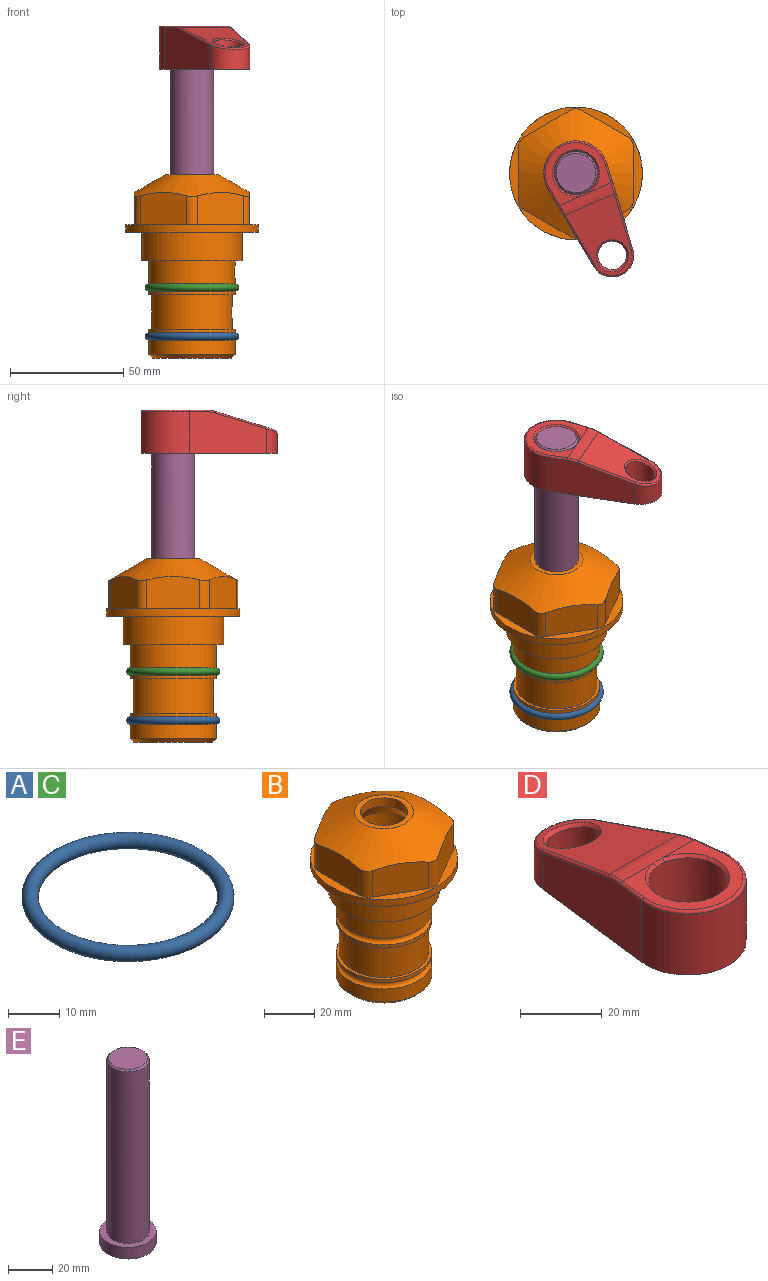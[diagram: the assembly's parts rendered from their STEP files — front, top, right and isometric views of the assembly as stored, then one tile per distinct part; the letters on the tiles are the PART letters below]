
ASSEMBLY  parts=5 mates=4
PART A: 1 faces, bbox 44.7x44.7x3.2 mm
  f0: torus R=19.05mm, axis (0,0,1), area 1193.9mm2
PART B: 36 faces, bbox 58.7x58.7x81 mm
  f0: cylinder r=17.78mm len=35.56mm, axis (0,0,1), area 1670.8mm2, adj f23,f24,f31
  f1: cylinder r=19.05mm len=38.1mm, axis (0,0,1), area 1191.9mm2, adj f26,f27,f30
  f2: plane 58.66x58.66mm, normal (0,0,-1), area 1150.6mm2, adj f3,f28
  f3: cylinder r=29.33mm len=58.66mm, axis (0,0,-1), area 585.1mm2, adj f2,f4
  f4: plane 58.66x58.66mm, normal (0,0,1), area 475.9mm2, adj f3,f5,f6,f7,f8,f9,f10,f11
  f5: plane 20.32x14.34mm, normal (-0.5,0.87,0), area 324.4mm2, adj f4,f15,f16,f17
  f6: plane 20.32x14.34mm, normal (0.5,0.87,0), area 324.4mm2, adj f4,f14,f15,f17
  f7: plane 23.48x14.34mm, normal (1,0,0), area 324.4mm2, adj f4,f13,f14,f17
  f8: plane 20.32x14.34mm, normal (0.5,-0.87,0), area 324.4mm2, adj f4,f12,f13,f17
  f9: plane 20.32x14.34mm, normal (-0.5,-0.87,0), area 324.4mm2, adj f4,f11,f12,f17
  f10: plane 23.48x14.34mm, normal (-1,0,0), area 324.4mm2, adj f4,f11,f16,f17
  f11: cylinder r=5.08mm len=12.85mm, axis (0,0,-1), area 67.2mm2, adj f4,f9,f10,f17
  f12: cylinder r=5.08mm len=12.85mm, axis (0,0,-1), area 67.2mm2, adj f4,f8,f9,f17
  f13: cylinder r=5.08mm len=12.85mm, axis (0,0,-1), area 67.2mm2, adj f4,f7,f8,f17
  f14: cylinder r=5.08mm len=12.85mm, axis (0,0,-1), area 67.2mm2, adj f4,f6,f7,f17
  f15: cylinder r=5.08mm len=12.85mm, axis (0,0,-1), area 67.2mm2, adj f4,f5,f6,f17
  f16: cylinder r=5.08mm len=12.85mm, axis (0,0,-1), area 67.2mm2, adj f4,f5,f10,f17
  f17: cone r=11.73mm half-angle=60deg, axis (0,0,-1), area 2071.8mm2, adj f5,f6,f7,f8,f9,f10,f11,f12
  f18: plane 23.46x23.46mm, normal (0,0,1), area 147.4mm2, adj f17,f35
  f19: plane 34.93x34.93mm, normal (0,0,-1), area 958mm2, adj f29
  f20: cylinder r=19.05mm len=38.1mm, axis (0,0,1), area 760.1mm2, adj f21,f29
  f21: torus R=19.05mm, axis (0,0,1), area 565.3mm2, adj f20,f22
  f22: cylinder r=19.05mm len=38.1mm, axis (0,0,1), area 190mm2, adj f21,f23
  f23: plane 38.1x38.1mm, normal (0,0,1), area 146.9mm2, adj f0,f22
  f24: plane 38.1x38.1mm, normal (0,0,-1), area 146.9mm2, adj f0,f25
  f25: cylinder r=19.05mm len=38.1mm, axis (0,0,1), area 190mm2, adj f24,f26
  f26: torus R=19.05mm, axis (0,0,1), area 565.3mm2, adj f1,f25
  f27: plane 44.45x44.45mm, normal (0,0,-1), area 411.7mm2, adj f1,f28
  f28: cylinder r=22.23mm len=44.45mm, axis (0,0,1), area 1773.5mm2, adj f2,f27
  f29: cone r=19.05mm half-angle=45deg, axis (0,0,1), area 257.5mm2, adj f19,f20
  f30: cylinder r=3.17mm len=6.75mm, axis (-1,0,0), area 128mm2, adj f1,f33
  f31: cylinder r=3.17mm len=6.35mm, axis (-1,0,0), area 102.5mm2, adj f0,f33
  f32: plane 25.4x25.4mm, normal (0,0,1), area 506.7mm2, adj f33
  f33: cylinder r=12.7mm len=66.42mm, axis (0,0,-1), area 5236.2mm2, adj f30,f31,f32,f34
  f34: cone r=9.53mm half-angle=30deg, axis (0,0,-1), area 443.4mm2, adj f33,f35
  f35: cylinder r=9.53mm len=19.05mm, axis (0,0,-1), area 240.9mm2, adj f18,f34
PART C: same geometry as A
PART D: 31 faces, bbox 31.7x65.5x19.8 mm
  f0: plane 39.12x18.26mm, normal (0.99,0.12,0), area 612.2mm2, adj f1,f4,f7,f11,f13,f15
  f1: cylinder r=9.53mm len=18.91mm, axis (0,0,-1), area 296.1mm2, adj f0,f2,f7,f17
  f2: plane 39.12x18.26mm, normal (-0.99,0.12,0), area 612.2mm2, adj f1,f4,f7,f12,f14,f16
  f3: cylinder r=6.35mm len=12.7mm, axis (0,0,-1), area 362.4mm2, adj f7,f18
  f4: cylinder r=14.29mm len=28.58mm, axis (0,0,-1), area 882.2mm2, adj f0,f2,f7,f10
  f5: cylinder r=9.53mm len=19.05mm, axis (0,0,-1), area 1092.6mm2, adj f7,f19,f20
  f6: plane 26.99x23.69mm, normal (0,0,1), area 216.2mm2, adj f9,f10,f11,f12,f19
  f7: plane 63.5x28.58mm, normal (0,0,-1), area 661.8mm2, adj f0,f1,f2,f3,f4,f5,f22,f23
  f8: plane 33.52x23.6mm, normal (0,0.26,0.97), area 486mm2, adj f9,f15,f16,f17,f18
  f9: cylinder r=19.05mm len=24.72mm, axis (1,0,0), area 120.4mm2, adj f6,f8,f13,f14,f20
  f10: torus R=13.49mm, axis (0,0,1), area 59mm2, adj f4,f6,f11,f12
  f11: cylinder r=0.79mm len=8.67mm, axis (0.12,-0.99,0), area 10.8mm2, adj f0,f6,f10,f13
  f12: cylinder r=0.79mm len=8.67mm, axis (0.12,0.99,0), area 10.8mm2, adj f2,f6,f10,f14
  f13: bspline ~4.95x1.42mm, area 6.1mm2, adj f0,f9,f11,f15
  f14: bspline ~4.95x1.42mm, area 6.1mm2, adj f2,f9,f12,f16
  f15: cylinder r=0.79mm len=25.95mm, axis (0.12,-0.96,0.26), area 32.9mm2, adj f0,f8,f13,f17
  f16: cylinder r=0.79mm len=25.95mm, axis (0.12,0.96,-0.26), area 32.9mm2, adj f2,f8,f14,f17
  f17: bspline ~18.91x8.38mm, area 30mm2, adj f1,f8,f15,f16
  f18: bspline ~14.29x14.29mm, area 48.3mm2, adj f3,f8
  f19: cone r=9.53mm half-angle=45deg, axis (0,0,1), area 66.5mm2, adj f5,f6,f20
  f20: bspline ~3.22x0.96mm, area 3.5mm2, adj f5,f9,f19
  f21: plane 2.75x2.72mm, normal (0,0,-1), area 2.9mm2, adj f23,f25,f28
  f22: plane 23.05x15.88mm, normal (-0.99,-0.12,0), area 323.6mm2, adj f7,f25,f26,f27,f28,f29
  f23: plane 23.05x15.88mm, normal (0.99,-0.12,0), area 323.6mm2, adj f7,f21,f25,f27,f28,f30
  f24: cylinder r=9.53mm len=10.69mm, axis (0,0,-1), area 114.7mm2, adj f7,f27,f29,f30
  f25: cylinder r=12.7mm len=20.59mm, axis (0,0,-1), area 381.1mm2, adj f7,f21,f22,f23,f26,f28
  f26: plane 2.75x2.72mm, normal (0,0,-1), area 2.9mm2, adj f22,f25,f28
  f27: plane 19.72x18.37mm, normal (0,-0.26,-0.97), area 291.8mm2, adj f22,f23,f24,f28,f29,f30
  f28: cylinder r=15.88mm len=19.92mm, axis (1,0,0), area 54.8mm2, adj f21,f22,f23,f25,f26,f27
  f29: cylinder r=1.59mm len=11mm, axis (0,0,-1), area 34.7mm2, adj f7,f22,f24,f27
  f30: cylinder r=1.59mm len=11mm, axis (0,0,-1), area 34.7mm2, adj f7,f23,f24,f27
PART E: 6 faces, bbox 25.4x25.4x101.6 mm
  f0: plane 17.46x17.46mm, normal (0,0,1), area 239.5mm2, adj f5
  f1: plane 25.4x25.4mm, normal (0,0,-1), area 506.7mm2, adj f2
  f2: cylinder r=12.7mm len=25.4mm, axis (0,0,1), area 506.7mm2, adj f1,f3
  f3: plane 25.4x25.4mm, normal (0,0,1), area 221.7mm2, adj f2,f4
  f4: cylinder r=9.53mm len=94.46mm, axis (0,0,1), area 5653mm2, adj f3,f5
  f5: cone r=8.73mm half-angle=45deg, axis (0,0,-1), area 64.4mm2, adj f0,f4
PLACE A rot(axis=(0,0,-1),0deg) t=(0,0,-21.59)mm
PLACE B rot(axis=(0,0,-1),0deg) t=(0,0,0)mm fixed
PLACE C rot(axis=(0,0,-1),0deg) t=(0,0,0)mm
PLACE D rot(axis=(0,0,-1),156.3deg) t=(0,0,27.55)mm
PLACE E rot(axis=(0,0,-1),156.3deg) t=(0,0,27.55)mm
MATE cylindrical E.f2 <-> B.f0  axis (0,0,-1) through (0,0,-10.55)mm
MATE fastened E.f2 <-> D.f4  axis (0,0,1) through (0,0,91.05)mm
MATE fastened A.f0 <-> B.f0  axis (0,0,1) through (0,0,-46.1)mm
MATE fastened C.f0 <-> B.f0  axis (0,0,1) through (0,0,-24.51)mm
